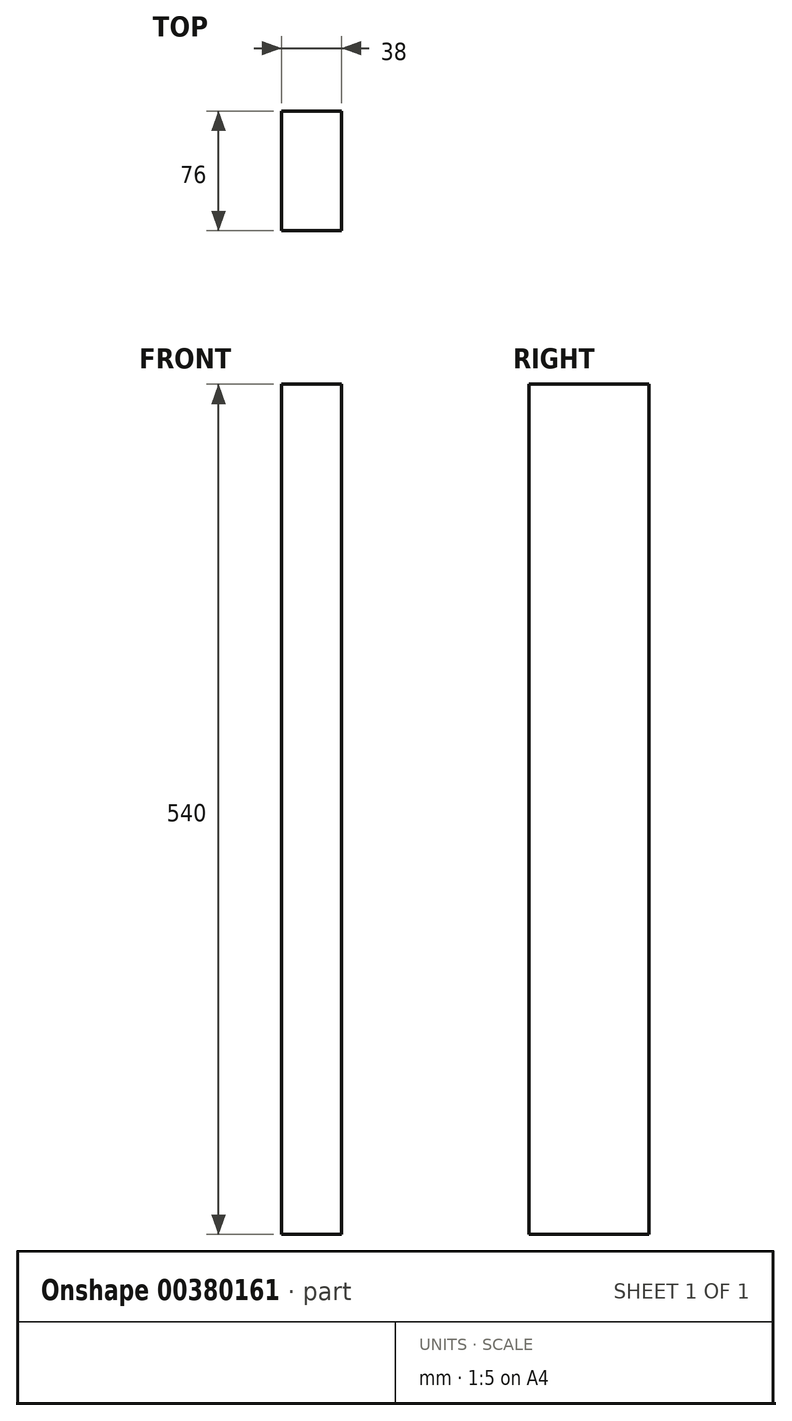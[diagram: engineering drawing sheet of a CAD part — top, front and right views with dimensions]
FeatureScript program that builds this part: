
annotation { "Feature Type Name" : "Feature", "Feature Type Description" : "" }
export const myFeature = defineFeature(function(context is Context, id is Id, definition is map)
    precondition{}
    {
        {
            var Q0;
            Q0=qCreatedBy(makeId("Top.planeOp"),FACE);
            var sketch = newSketch(context, id + "F0", { "sketchPlane" : qUnion([Q0])});
            skLineSegment(sketch, "E0.bottom", {"start": v(19, -38) * mm, "end": v(-19, -38) * mm});
            skLineSegment(sketch, "E0.top", {"start": v(19, 38) * mm, "end": v(-19, 38) * mm});
            skLineSegment(sketch, "E0.left", {"start": v(19, -38) * mm, "end": v(19, 38) * mm});
            skLineSegment(sketch, "E0.right", {"start": v(-19, -38) * mm, "end": v(-19, 38) * mm});
            skPoint(sketch, "E0.middle", {"position": v(0, 0) * mm});
            skSolve(sketch);
        }
        {
            var Q0;
            Q0 = qSketchRegion(id + "F0", true);
            extrude(context, id + "F1", {"entities" : qUnion([Q0]), "depth" : 540 * mm});
        }
    });
